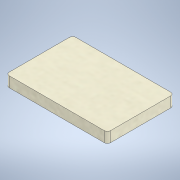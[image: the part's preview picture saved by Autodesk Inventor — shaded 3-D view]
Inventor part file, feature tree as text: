
AUTODESK INVENTOR PART (.ipt)
format: ipt  version: 2021 (Build 250183000, 183)  size: 112,128 bytes
history: native  units: mm
features: extrude x1, sketch x1
ambient origin geometry x8: Origin, YZ Plane, XZ Plane, XY Plane, X Axis, Y Axis, Z Axis, Center Point
bodies: Solid1 (feature_tree)
feature tree (2):
  extrude  "Extrusion1"  Depth=42.0mm
  sketch  "Sketch1"  dims[d0=64.0mm d1=42.0mm d2=2.0mm d3=6.6mm d4=0.0mm]
